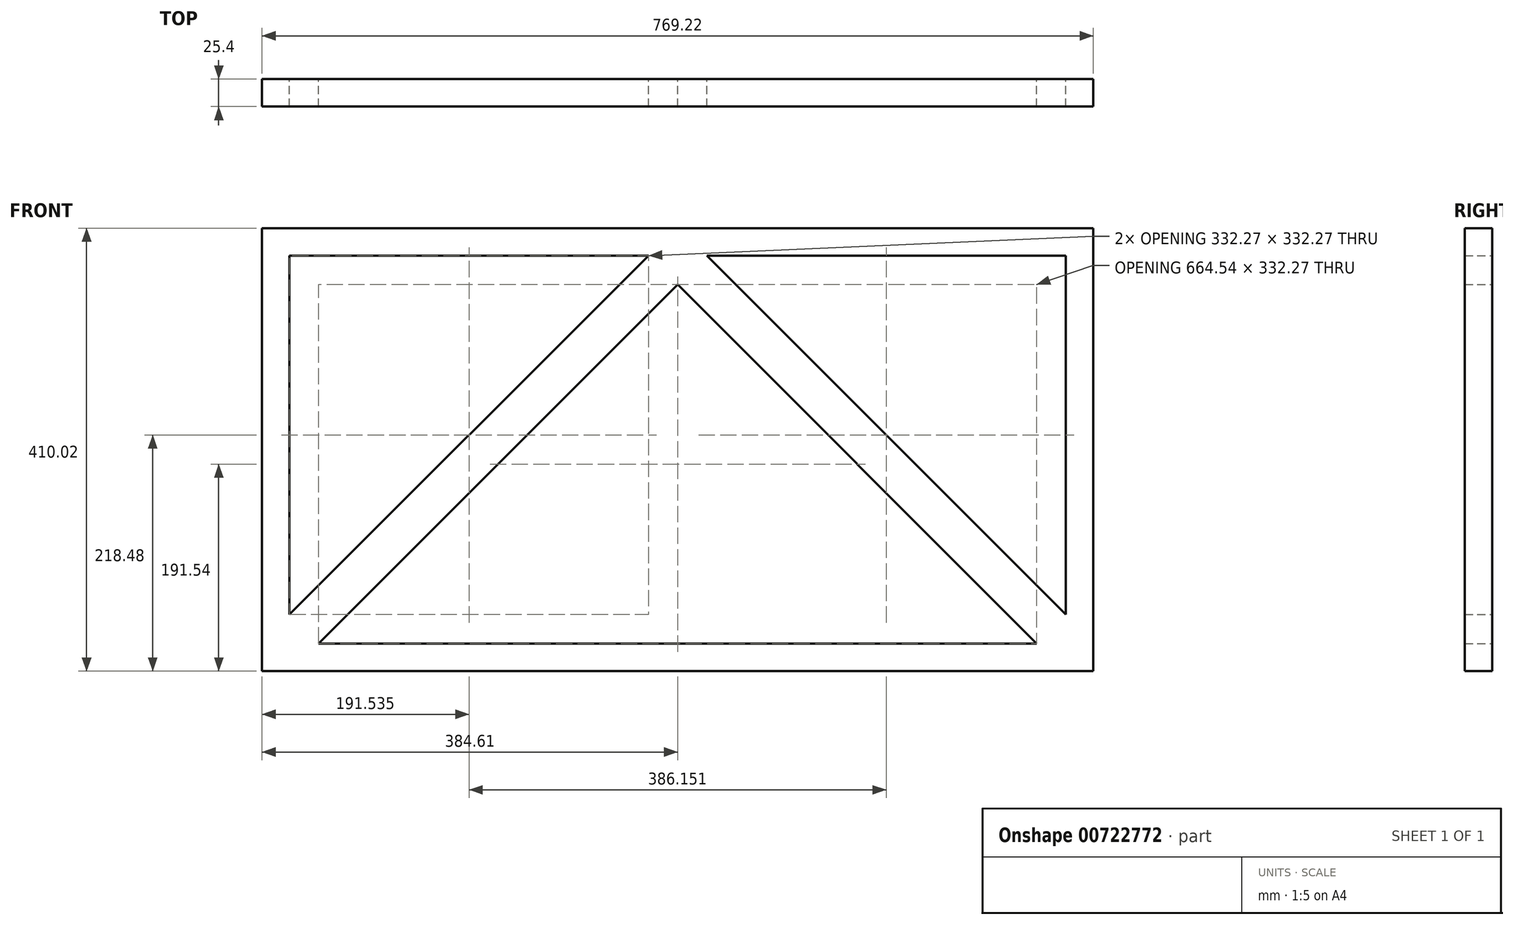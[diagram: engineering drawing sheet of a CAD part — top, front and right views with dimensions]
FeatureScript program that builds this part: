
annotation { "Feature Type Name" : "Feature", "Feature Type Description" : "" }
export const myFeature = defineFeature(function(context is Context, id is Id, definition is map)
    precondition{}
    {
        {
            var Q0;
            Q0=qCreatedBy(makeId("Front.planeOp"),FACE);
            var sketch = newSketch(context, id + "F0", { "sketchPlane" : qUnion([Q0])});
            skLineSegment(sketch, "E0", {"start": v(-359.21, -152.66) * mm, "end": v(-359.21, -179.6) * mm});
            skLineSegment(sketch, "E1", {"start": v(-359.21, -179.6) * mm, "end": v(-332.27, -179.6) * mm});
            skLineSegment(sketch, "E2", {"start": v(-332.27, -179.6) * mm, "end": v(0, 152.66) * mm});
            skLineSegment(sketch, "E3", {"start": v(0, 152.66) * mm, "end": v(0, 179.6) * mm});
            skLineSegment(sketch, "E4", {"start": v(0, 179.6) * mm, "end": v(-26.94, 179.6) * mm});
            skLineSegment(sketch, "E5", {"start": v(-26.94, 179.6) * mm, "end": v(-359.21, -152.66) * mm});
            skLineSegment(sketch, "E6", {"start": v(0, 179.6) * mm, "end": v(26.94, 179.6) * mm});
            skLineSegment(sketch, "E7", {"start": v(26.94, 179.6) * mm, "end": v(359.21, -152.66) * mm});
            skLineSegment(sketch, "E8", {"start": v(359.21, -152.66) * mm, "end": v(359.21, -179.6) * mm});
            skLineSegment(sketch, "E9", {"start": v(359.21, -179.6) * mm, "end": v(332.27, -179.6) * mm});
            skLineSegment(sketch, "E10", {"start": v(332.27, -179.6) * mm, "end": v(0, 152.66) * mm});
            skLineSegment(sketch, "E11.bottom", {"start": v(359.21, 179.6) * mm, "end": v(-359.21, 179.6) * mm});
            skLineSegment(sketch, "E11.top", {"start": v(359.21, -179.6) * mm, "end": v(-359.21, -179.6) * mm});
            skLineSegment(sketch, "E11.left", {"start": v(359.21, 179.6) * mm, "end": v(359.21, -179.6) * mm});
            skLineSegment(sketch, "E11.right", {"start": v(-359.21, 179.6) * mm, "end": v(-359.21, -179.6) * mm});
            skPoint(sketch, "E11.middle", {"position": v(0, 0) * mm});
            skLineSegment(sketch, "E12", {"start": v(0, 179.6) * mm, "end": v(0, -179.6) * mm, "construction": true});
            skLineSegment(sketch, "E13.bottom", {"start": v(384.61, 205) * mm, "end": v(-384.61, 205) * mm});
            skLineSegment(sketch, "E13.top", {"start": v(384.61, -205) * mm, "end": v(-384.61, -205) * mm});
            skLineSegment(sketch, "E13.left", {"start": v(384.61, 205) * mm, "end": v(384.61, -205) * mm});
            skLineSegment(sketch, "E13.right", {"start": v(-384.61, 205) * mm, "end": v(-384.61, -205) * mm});
            skLineSegment(sketch, "E14", {"start": v(-359.21, 179.6) * mm, "end": v(-384.61, 179.6) * mm, "construction": true});
            skLineSegment(sketch, "E15", {"start": v(-384.61, 179.6) * mm, "end": v(-384.61, 205) * mm, "construction": true});
            skLineSegment(sketch, "E16", {"start": v(-359.21, -152.66) * mm, "end": v(-332.27, -179.6) * mm, "construction": true});
            skLineSegment(sketch, "E17", {"start": v(-359.21, -179.6) * mm, "end": v(0, 179.6) * mm, "construction": true});
            skSolve(sketch);
        }
        {
            var Q0;
            Q0=makeQuery(id+"F0.imprint","IMPRINT",FACE,{"disambiguationData":[TD([[makeQuery(id+"F0.imprint","IMPRINT",EDGE,{"derivedFrom":sQuery(id+"F0.wireOp",EDGE,"E13.bottom")}),1.0]])]});
            var Q1;
            {var subQ3=sQuery(id+"F0.wireOp",EDGE,"E2");Q1=makeQuery(id+"F0.imprint","IMPRINT",FACE,{"disambiguationData":[TD([[makeQuery(id+"F0.imprint","IMPRINT",EDGE,{"derivedFrom":subQ3}),1.0]])]});}
            var Q2;
            {var subQ3=sQuery(id+"F0.wireOp",EDGE,"E3");Q2=makeQuery(id+"F0.imprint","IMPRINT",FACE,{"disambiguationData":[TD([[makeQuery(id+"F0.imprint","IMPRINT",EDGE,{"derivedFrom":subQ3}),-1.0]])]});}
            extrude(context, id + "F1", {"entities" : qUnion([Q0, Q1, Q2]), "depth" : 25.4 * mm, "offsetDistance" : 25.4 * mm});
        }
    });
